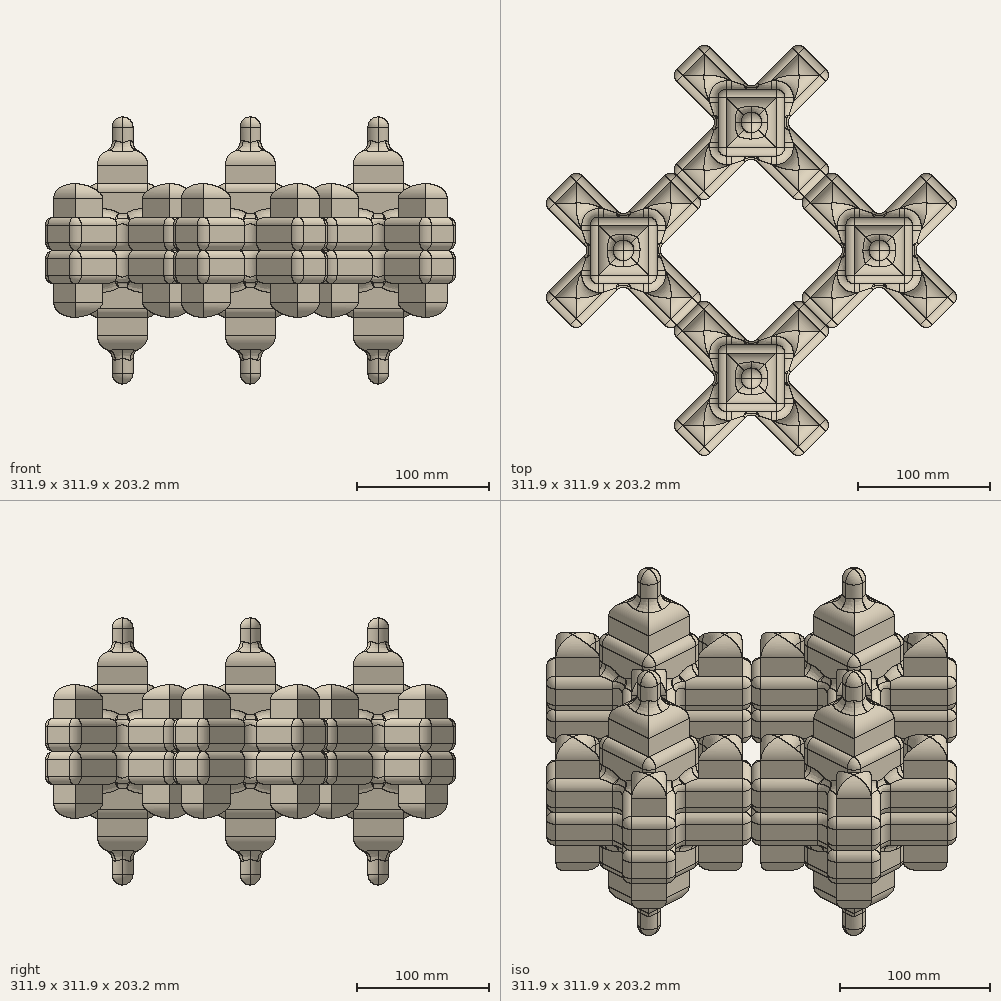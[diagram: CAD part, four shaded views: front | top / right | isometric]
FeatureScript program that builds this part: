
annotation { "Feature Type Name" : "Feature", "Feature Type Description" : "" }
export const myFeature = defineFeature(function(context is Context, id is Id, definition is map)
    precondition{}
    {
        {
            var Q0;
            Q0=qCreatedBy(makeId("Top.planeOp"),FACE);
            var sketch = newSketch(context, id + "F0", { "sketchPlane" : qUnion([Q0])});
            skLineSegment(sketch, "E0.bottom", {"start": v(0, 0) * mm, "end": v(50.8, 0) * mm});
            skLineSegment(sketch, "E0.top", {"start": v(0, 50.8) * mm, "end": v(50.8, 50.8) * mm});
            skLineSegment(sketch, "E0.left", {"start": v(0, 0) * mm, "end": v(0, 50.8) * mm});
            skLineSegment(sketch, "E0.right", {"start": v(50.8, 0) * mm, "end": v(50.8, 50.8) * mm});
            skLineSegment(sketch, "E1", {"start": v(0, 25.4) * mm, "end": v(-35.92, -10.52) * mm});
            skLineSegment(sketch, "E2", {"start": v(25.4, 0) * mm, "end": v(-10.52, -35.92) * mm});
            skLineSegment(sketch, "E3", {"start": v(-35.92, -10.52) * mm, "end": v(-10.52, -35.92) * mm});
            skLineSegment(sketch, "E4", {"start": v(0, 25.4) * mm, "end": v(-35.92, 61.32) * mm});
            skLineSegment(sketch, "E5", {"start": v(25.4, 0) * mm, "end": v(61.32, -35.92) * mm});
            skLineSegment(sketch, "E6", {"start": v(50.8, 25.4) * mm, "end": v(86.72, -10.52) * mm});
            skLineSegment(sketch, "E7", {"start": v(86.72, -10.52) * mm, "end": v(61.32, -35.92) * mm});
            skLineSegment(sketch, "E8", {"start": v(25.4, 50.8) * mm, "end": v(-10.52, 86.72) * mm});
            skLineSegment(sketch, "E9", {"start": v(-10.52, 86.72) * mm, "end": v(-35.92, 61.32) * mm});
            skLineSegment(sketch, "E10", {"start": v(25.4, 50.8) * mm, "end": v(61.32, 86.72) * mm});
            skLineSegment(sketch, "E11", {"start": v(50.8, 25.4) * mm, "end": v(86.72, 61.32) * mm});
            skLineSegment(sketch, "E12", {"start": v(86.72, 61.32) * mm, "end": v(61.32, 86.72) * mm});
            skSolve(sketch);
        }
        {
            var Q0;
            {var subQ4=sQuery(id+"F0.wireOp",EDGE,"E0.left");var subQ6=sQuery(id+"F0.wireOp",EDGE,"E0.bottom");var subQ9=makeQuery(id+"F0.imprint","INTERSECT",VERTEX,{"derivedFrom":[subQ6,subQ4]});Q0=makeQuery(id+"F0.imprint","IMPRINT",FACE,{"disambiguationData":[TD([[makeQuery(id+"F0.imprint","IMPRINT",EDGE,{"disambiguationData":[TD([[subQ9,-1.0]])],"derivedFrom":subQ6}),1.0]])]});}
            extrude(context, id + "F1", {"entities" : qUnion([Q0]), "depth" : 50.8 * mm});
        }
        {
            var Q0;
            {var subQ0=sQuery(id+"F0.wireOp",EDGE,"E1");Q0=makeQuery(id+"F0.imprint","IMPRINT",FACE,{"disambiguationData":[TD([[makeQuery(id+"F0.imprint","IMPRINT",EDGE,{"derivedFrom":subQ0}),1.0]])]});}
            var Q1;
            {var subQ1=sQuery(id+"F0.wireOp",EDGE,"E5");Q1=makeQuery(id+"F0.imprint","IMPRINT",FACE,{"disambiguationData":[TD([[makeQuery(id+"F0.imprint","IMPRINT",EDGE,{"derivedFrom":subQ1}),1.0]])]});}
            var Q2;
            {var subQ0=sQuery(id+"F0.wireOp",EDGE,"E10");Q2=makeQuery(id+"F0.imprint","IMPRINT",FACE,{"disambiguationData":[TD([[makeQuery(id+"F0.imprint","IMPRINT",EDGE,{"derivedFrom":subQ0}),-1.0]])]});}
            var Q3;
            {var subQ0=sQuery(id+"F0.wireOp",EDGE,"E4");Q3=makeQuery(id+"F0.imprint","IMPRINT",FACE,{"disambiguationData":[TD([[makeQuery(id+"F0.imprint","IMPRINT",EDGE,{"derivedFrom":subQ0}),-1.0]])]});}
            extrude(context, id + "F2", {"entities" : qUnion([Q0, Q1, Q2, Q3]), "operationType" : NewBodyOperationType.ADD, "depth" : 25.4 * mm});
        }
        {
            var Q0;
            Q0=makeQuery(id+"F2.opExtrude","SWEPT_FACE",FACE,{"disambiguationData":[OSD([sQuery(id+"F0.wireOp",EDGE,"E4")])]});
            var Q1;
            Q1=makeQuery(id+"F2.opExtrude","SWEPT_FACE",FACE,{"disambiguationData":[OSD([sQuery(id+"F0.wireOp",EDGE,"E1")])]});
            var Q2;
            Q2=makeQuery(id+"F2.opExtrude","SWEPT_FACE",FACE,{"disambiguationData":[OSD([sQuery(id+"F0.wireOp",EDGE,"E2")])]});
            var Q3;
            Q3=makeQuery(id+"F2.opExtrude","SWEPT_FACE",FACE,{"disambiguationData":[OSD([sQuery(id+"F0.wireOp",EDGE,"E5")])]});
            var Q4;
            Q4=makeQuery(id+"F2.opExtrude","SWEPT_FACE",FACE,{"disambiguationData":[OSD([sQuery(id+"F0.wireOp",EDGE,"E3")])]});
            var Q5;
            Q5=makeQuery(id+"F2.opExtrude","SWEPT_FACE",FACE,{"disambiguationData":[OSD([sQuery(id+"F0.wireOp",EDGE,"E7")])]});
            var Q6;
            Q6=makeQuery(id+"F2.opExtrude","SWEPT_FACE",FACE,{"disambiguationData":[OSD([sQuery(id+"F0.wireOp",EDGE,"E6")])]});
            var Q7;
            Q7=makeQuery(id+"F2.opExtrude","SWEPT_FACE",FACE,{"disambiguationData":[OSD([sQuery(id+"F0.wireOp",EDGE,"E11")])]});
            var Q8;
            Q8=makeQuery(id+"F2.opExtrude","SWEPT_FACE",FACE,{"disambiguationData":[OSD([sQuery(id+"F0.wireOp",EDGE,"E12")])]});
            var Q9;
            Q9=makeQuery(id+"F2.opExtrude","SWEPT_FACE",FACE,{"disambiguationData":[OSD([sQuery(id+"F0.wireOp",EDGE,"E9")])]});
            var Q10;
            Q10=makeQuery(id+"F2.opExtrude","SWEPT_FACE",FACE,{"disambiguationData":[OSD([sQuery(id+"F0.wireOp",EDGE,"E8")])]});
            var Q11;
            Q11=makeQuery(id+"F2.opExtrude","SWEPT_FACE",FACE,{"disambiguationData":[OSD([sQuery(id+"F0.wireOp",EDGE,"E10")])]});
            fillet(context, id + "F3", {"entities" : qUnion([Q0, Q1, Q2, Q3, Q4, Q5, Q6, Q7, Q8, Q9, Q10, Q11]), "radius" : 6.35 * mm, "tangentPropagation" : true, "allowEdgeOverflow" : false});
        }
        {
            var Q0;
            Q0=makeQuery(id+"F1.opExtrude","SWEPT_FACE",FACE,{"disambiguationData":[OSD([sQuery(id+"F0.wireOp",EDGE,"E0.bottom")])]});
            var Q1;
            Q1=makeQuery(id+"F1.opExtrude","SWEPT_FACE",FACE,{"disambiguationData":[OSD([sQuery(id+"F0.wireOp",EDGE,"E0.right")])]});
            var Q2;
            Q2=makeQuery(id+"F1.opExtrude","SWEPT_FACE",FACE,{"disambiguationData":[OSD([sQuery(id+"F0.wireOp",EDGE,"E0.top")])]});
            var Q3;
            Q3=makeQuery(id+"F1.opExtrude","SWEPT_FACE",FACE,{"disambiguationData":[OSD([sQuery(id+"F0.wireOp",EDGE,"E0.left")])]});
            var Q4;
            Q4=makeQuery(id+"F1.opExtrude","CAP_FACE",FACE,{"disambiguationData":[OSD([sQuery(id+"F0.wireOp",EDGE,"E0.bottom"),sQuery(id+"F0.wireOp",EDGE,"E0.top"),sQuery(id+"F0.wireOp",EDGE,"E0.left"),sQuery(id+"F0.wireOp",EDGE,"E0.right")])],"isStart":false});
            fillet(context, id + "F4", {"entities" : qUnion([Q0, Q1, Q2, Q3, Q4]), "radius" : 6.35 * mm, "tangentPropagation" : true, "allowEdgeOverflow" : false});
        }
        {
            var Q0;
            Q0=makeQuery(id+"F1.opExtrude","CAP_FACE",FACE,{"disambiguationData":[OSD([sQuery(id+"F0.wireOp",EDGE,"E0.bottom"),sQuery(id+"F0.wireOp",EDGE,"E0.top"),sQuery(id+"F0.wireOp",EDGE,"E0.left"),sQuery(id+"F0.wireOp",EDGE,"E0.right")])],"isStart":false});
            var Q1;
            Q1=makeQuery(id+"F2.opExtrude","CAP_FACE",FACE,{"disambiguationData":[OSD([sQuery(id+"F0.wireOp",EDGE,"E0.bottom"),sQuery(id+"F0.wireOp",EDGE,"E0.left"),sQuery(id+"F0.wireOp",EDGE,"E1"),sQuery(id+"F0.wireOp",EDGE,"E2"),sQuery(id+"F0.wireOp",EDGE,"E3")])],"isStart":false});
            var Q2;
            Q2=makeQuery(id+"F2.opExtrude","CAP_FACE",FACE,{"disambiguationData":[OSD([sQuery(id+"F0.wireOp",EDGE,"E0.bottom"),sQuery(id+"F0.wireOp",EDGE,"E0.right"),sQuery(id+"F0.wireOp",EDGE,"E5"),sQuery(id+"F0.wireOp",EDGE,"E6"),sQuery(id+"F0.wireOp",EDGE,"E7")])],"isStart":false});
            var Q3;
            Q3=makeQuery(id+"F2.opExtrude","CAP_FACE",FACE,{"disambiguationData":[OSD([sQuery(id+"F0.wireOp",EDGE,"E0.top"),sQuery(id+"F0.wireOp",EDGE,"E0.left"),sQuery(id+"F0.wireOp",EDGE,"E4"),sQuery(id+"F0.wireOp",EDGE,"E8"),sQuery(id+"F0.wireOp",EDGE,"E9")])],"isStart":false});
            var Q4;
            Q4=makeQuery(id+"F2.opExtrude","CAP_FACE",FACE,{"disambiguationData":[OSD([sQuery(id+"F0.wireOp",EDGE,"E0.top"),sQuery(id+"F0.wireOp",EDGE,"E0.right"),sQuery(id+"F0.wireOp",EDGE,"E10"),sQuery(id+"F0.wireOp",EDGE,"E11"),sQuery(id+"F0.wireOp",EDGE,"E12")])],"isStart":false});
            extrude(context, id + "F5", {"entities" : qUnion([Q0, Q1, Q2, Q3, Q4]), "operationType" : NewBodyOperationType.ADD, "depth" : 25.4 * mm});
        }
        {
            var Q0;
            Q0=makeQuery(id+"F5.opExtrude","CAP_FACE",FACE,{"disambiguationData":[OSD([sQuery(id+"F0.wireOp",EDGE,"E0.bottom"),sQuery(id+"F0.wireOp",EDGE,"E0.top"),sQuery(id+"F0.wireOp",EDGE,"E0.left"),sQuery(id+"F0.wireOp",EDGE,"E0.right")])],"isStart":false});
            var Q1;
            Q1=makeQuery(id+"F5.opExtrude","CAP_FACE",FACE,{"disambiguationData":[OSD([sQuery(id+"F0.wireOp",EDGE,"E0.bottom"),sQuery(id+"F0.wireOp",EDGE,"E0.left"),sQuery(id+"F0.wireOp",EDGE,"E1"),sQuery(id+"F0.wireOp",EDGE,"E2"),sQuery(id+"F0.wireOp",EDGE,"E3")])],"isStart":false});
            var Q2;
            Q2=makeQuery(id+"F5.opExtrude","CAP_FACE",FACE,{"disambiguationData":[OSD([sQuery(id+"F0.wireOp",EDGE,"E0.top"),sQuery(id+"F0.wireOp",EDGE,"E0.left"),sQuery(id+"F0.wireOp",EDGE,"E4"),sQuery(id+"F0.wireOp",EDGE,"E8"),sQuery(id+"F0.wireOp",EDGE,"E9")])],"isStart":false});
            var Q3;
            Q3=makeQuery(id+"F5.opExtrude","CAP_FACE",FACE,{"disambiguationData":[OSD([sQuery(id+"F0.wireOp",EDGE,"E0.top"),sQuery(id+"F0.wireOp",EDGE,"E0.right"),sQuery(id+"F0.wireOp",EDGE,"E10"),sQuery(id+"F0.wireOp",EDGE,"E11"),sQuery(id+"F0.wireOp",EDGE,"E12")])],"isStart":false});
            var Q4;
            Q4=makeQuery(id+"F5.opExtrude","CAP_FACE",FACE,{"disambiguationData":[OSD([sQuery(id+"F0.wireOp",EDGE,"E0.bottom"),sQuery(id+"F0.wireOp",EDGE,"E0.right"),sQuery(id+"F0.wireOp",EDGE,"E5"),sQuery(id+"F0.wireOp",EDGE,"E6"),sQuery(id+"F0.wireOp",EDGE,"E7")])],"isStart":false});
            fillet(context, id + "F6", {"entities" : qUnion([Q0, Q1, Q2, Q3, Q4]), "radius" : 11.18 * mm, "tangentPropagation" : true, "allowEdgeOverflow" : false});
        }
        {
            var Q0;
            Q0=makeQuery(id+"F5.opExtrude","CAP_FACE",FACE,{"disambiguationData":[OSD([sQuery(id+"F0.wireOp",EDGE,"E0.bottom"),sQuery(id+"F0.wireOp",EDGE,"E0.top"),sQuery(id+"F0.wireOp",EDGE,"E0.left"),sQuery(id+"F0.wireOp",EDGE,"E0.right")])],"isStart":false});
            extrude(context, id + "F7", {"entities" : qUnion([Q0]), "operationType" : NewBodyOperationType.ADD, "depth" : 25.4 * mm});
        }
        {
            var Q0;
            {var subQ0=sQuery(id+"F0.wireOp",EDGE,"E0.right");var subQ1=sQuery(id+"F0.wireOp",EDGE,"E0.left");var subQ2=sQuery(id+"F0.wireOp",EDGE,"E0.top");var subQ3=sQuery(id+"F0.wireOp",EDGE,"E0.bottom");Q0=makeQuery(id+"F7.opExtrude","SWEPT_FACE",FACE,{"disambiguationData":[OSD([subQ3,subQ2,subQ1,subQ0]),TDD([makeQuery(id+"F6.opFillet","BLEND_EDGE",EDGE,{"blendedFrom":[makeQuery(id+"F5.opExtrude","CAP_EDGE",EDGE,{"disambiguationData":[OSD([subQ3,subQ2,subQ1,subQ0]),TDD([makeQuery(id+"F4.opFillet","BLEND_EDGE",EDGE,{"blendedFrom":[makeQuery(id+"F1.opExtrude","CAP_EDGE",EDGE,{"disambiguationData":[OSD([subQ3])],"isStart":false}),makeQuery(id+"F1.opExtrude","CAP_FACE",FACE,{"disambiguationData":[OSD([subQ3,subQ2,subQ1,subQ0])],"isStart":false})],"blendedInto":[makeQuery(id+"F1.opExtrude","CAP_FACE",FACE,{"disambiguationData":[OSD([subQ3,subQ2,subQ1,subQ0])],"isStart":false})]})])],"isStart":false}),makeQuery(id+"F5.opExtrude","CAP_FACE",FACE,{"disambiguationData":[OSD([subQ3,subQ2,subQ1,subQ0])],"isStart":false})],"blendedInto":[makeQuery(id+"F5.opExtrude","CAP_FACE",FACE,{"disambiguationData":[OSD([subQ3,subQ2,subQ1,subQ0])],"isStart":false})]})])]});}
            var Q1;
            {var subQ0=sQuery(id+"F0.wireOp",EDGE,"E0.right");var subQ1=sQuery(id+"F0.wireOp",EDGE,"E0.left");var subQ2=sQuery(id+"F0.wireOp",EDGE,"E0.top");var subQ3=sQuery(id+"F0.wireOp",EDGE,"E0.bottom");Q1=makeQuery(id+"F7.opExtrude","SWEPT_FACE",FACE,{"disambiguationData":[OSD([subQ3,subQ2,subQ1,subQ0]),TDD([makeQuery(id+"F6.opFillet","BLEND_EDGE",EDGE,{"blendedFrom":[makeQuery(id+"F5.opExtrude","CAP_EDGE",EDGE,{"disambiguationData":[OSD([subQ3,subQ2,subQ1,subQ0]),TDD([makeQuery(id+"F4.opFillet","BLEND_EDGE",EDGE,{"blendedFrom":[makeQuery(id+"F1.opExtrude","CAP_EDGE",EDGE,{"disambiguationData":[OSD([subQ1])],"isStart":false}),makeQuery(id+"F1.opExtrude","CAP_FACE",FACE,{"disambiguationData":[OSD([subQ3,subQ2,subQ1,subQ0])],"isStart":false})],"blendedInto":[makeQuery(id+"F1.opExtrude","CAP_FACE",FACE,{"disambiguationData":[OSD([subQ3,subQ2,subQ1,subQ0])],"isStart":false})]})])],"isStart":false}),makeQuery(id+"F5.opExtrude","CAP_FACE",FACE,{"disambiguationData":[OSD([subQ3,subQ2,subQ1,subQ0])],"isStart":false})],"blendedInto":[makeQuery(id+"F5.opExtrude","CAP_FACE",FACE,{"disambiguationData":[OSD([subQ3,subQ2,subQ1,subQ0])],"isStart":false})]})])]});}
            var Q2;
            {var subQ0=sQuery(id+"F0.wireOp",EDGE,"E0.right");var subQ1=sQuery(id+"F0.wireOp",EDGE,"E0.left");var subQ2=sQuery(id+"F0.wireOp",EDGE,"E0.top");var subQ3=sQuery(id+"F0.wireOp",EDGE,"E0.bottom");Q2=makeQuery(id+"F7.opExtrude","SWEPT_FACE",FACE,{"disambiguationData":[OSD([subQ3,subQ2,subQ1,subQ0]),TDD([makeQuery(id+"F6.opFillet","BLEND_EDGE",EDGE,{"blendedFrom":[makeQuery(id+"F5.opExtrude","CAP_EDGE",EDGE,{"disambiguationData":[OSD([subQ3,subQ2,subQ1,subQ0]),TDD([makeQuery(id+"F4.opFillet","BLEND_EDGE",EDGE,{"blendedFrom":[makeQuery(id+"F1.opExtrude","CAP_EDGE",EDGE,{"disambiguationData":[OSD([subQ0])],"isStart":false}),makeQuery(id+"F1.opExtrude","CAP_FACE",FACE,{"disambiguationData":[OSD([subQ3,subQ2,subQ1,subQ0])],"isStart":false})],"blendedInto":[makeQuery(id+"F1.opExtrude","CAP_FACE",FACE,{"disambiguationData":[OSD([subQ3,subQ2,subQ1,subQ0])],"isStart":false})]})])],"isStart":false}),makeQuery(id+"F5.opExtrude","CAP_FACE",FACE,{"disambiguationData":[OSD([subQ3,subQ2,subQ1,subQ0])],"isStart":false})],"blendedInto":[makeQuery(id+"F5.opExtrude","CAP_FACE",FACE,{"disambiguationData":[OSD([subQ3,subQ2,subQ1,subQ0])],"isStart":false})]})])]});}
            var Q3;
            {var subQ0=sQuery(id+"F0.wireOp",EDGE,"E0.right");var subQ1=sQuery(id+"F0.wireOp",EDGE,"E0.left");var subQ2=sQuery(id+"F0.wireOp",EDGE,"E0.top");var subQ3=sQuery(id+"F0.wireOp",EDGE,"E0.bottom");Q3=makeQuery(id+"F7.opExtrude","SWEPT_FACE",FACE,{"disambiguationData":[OSD([subQ3,subQ2,subQ1,subQ0]),TDD([makeQuery(id+"F6.opFillet","BLEND_EDGE",EDGE,{"blendedFrom":[makeQuery(id+"F5.opExtrude","CAP_EDGE",EDGE,{"disambiguationData":[OSD([subQ3,subQ2,subQ1,subQ0]),TDD([makeQuery(id+"F4.opFillet","BLEND_EDGE",EDGE,{"blendedFrom":[makeQuery(id+"F1.opExtrude","CAP_EDGE",EDGE,{"disambiguationData":[OSD([subQ2])],"isStart":false}),makeQuery(id+"F1.opExtrude","CAP_FACE",FACE,{"disambiguationData":[OSD([subQ3,subQ2,subQ1,subQ0])],"isStart":false})],"blendedInto":[makeQuery(id+"F1.opExtrude","CAP_FACE",FACE,{"disambiguationData":[OSD([subQ3,subQ2,subQ1,subQ0])],"isStart":false})]})])],"isStart":false}),makeQuery(id+"F5.opExtrude","CAP_FACE",FACE,{"disambiguationData":[OSD([subQ3,subQ2,subQ1,subQ0])],"isStart":false})],"blendedInto":[makeQuery(id+"F5.opExtrude","CAP_FACE",FACE,{"disambiguationData":[OSD([subQ3,subQ2,subQ1,subQ0])],"isStart":false})]})])]});}
            fillet(context, id + "F8", {"entities" : qUnion([Q0, Q1, Q2, Q3]), "radius" : 7.82 * mm, "tangentPropagation" : true, "allowEdgeOverflow" : false});
        }
        {
            var Q0;
            Q0=makeQuery(id+"F1.opExtrude","SWEPT_BODY",BODY,{"disambiguationData":[OSD([sQuery(id+"F0.wireOp",EDGE,"E0.bottom"),sQuery(id+"F0.wireOp",EDGE,"E0.top"),sQuery(id+"F0.wireOp",EDGE,"E0.left"),sQuery(id+"F0.wireOp",EDGE,"E0.right")])]});
            var Q1;
            Q1=qCreatedBy(makeId("Top.planeOp"),FACE);
            mirror(context, id + "F9", {"operationType" : NewBodyOperationType.ADD, "entities" : qUnion([Q0]), "mirrorPlane" : qUnion([Q1])});
        }
        {
            var Q0;
            Q0=makeQuery(id+"F1.opExtrude","SWEPT_BODY",BODY,{"disambiguationData":[OSD([sQuery(id+"F0.wireOp",EDGE,"E0.bottom"),sQuery(id+"F0.wireOp",EDGE,"E0.top"),sQuery(id+"F0.wireOp",EDGE,"E0.left"),sQuery(id+"F0.wireOp",EDGE,"E0.right")])]});
            var Q1;
            Q1=makeQuery(id+"F9.opPattern","COPY",FACE,{"derivedFrom":makeQuery(id+"F2.opExtrude","SWEPT_FACE",FACE,{"disambiguationData":[OSD([sQuery(id+"F0.wireOp",EDGE,"E7")])]}),"instanceName":"1"});
            mirror(context, id + "F10", {"operationType" : NewBodyOperationType.ADD, "entities" : qUnion([Q0]), "mirrorPlane" : qUnion([Q1])});
        }
        {
            var Q0;
            Q0=makeQuery(id+"F1.opExtrude","SWEPT_BODY",BODY,{"disambiguationData":[OSD([sQuery(id+"F0.wireOp",EDGE,"E0.bottom"),sQuery(id+"F0.wireOp",EDGE,"E0.top"),sQuery(id+"F0.wireOp",EDGE,"E0.left"),sQuery(id+"F0.wireOp",EDGE,"E0.right")])]});
            var Q1;
            Q1=makeQuery(id+"F9.opPattern","COPY",FACE,{"derivedFrom":makeQuery(id+"F2.opExtrude","SWEPT_FACE",FACE,{"disambiguationData":[OSD([sQuery(id+"F0.wireOp",EDGE,"E12")])]}),"instanceName":"1"});
            mirror(context, id + "F11", {"operationType" : NewBodyOperationType.ADD, "entities" : qUnion([Q0]), "mirrorPlane" : qUnion([Q1])});
        }
    });
